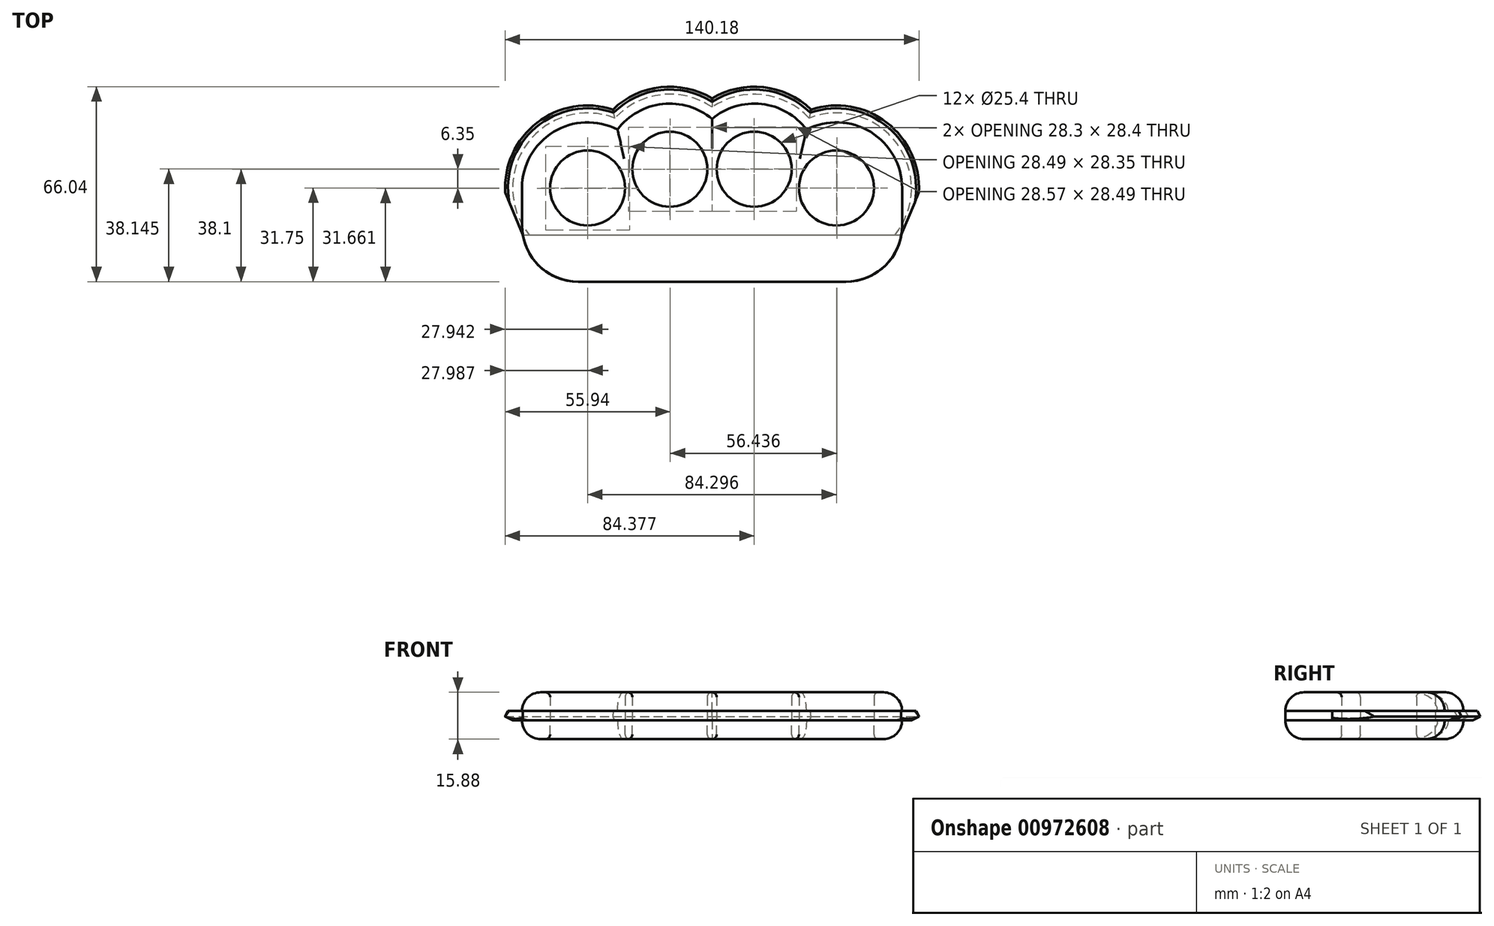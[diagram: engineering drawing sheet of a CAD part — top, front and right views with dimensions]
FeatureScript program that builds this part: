
annotation { "Feature Type Name" : "Feature", "Feature Type Description" : "" }
export const myFeature = defineFeature(function(context is Context, id is Id, definition is map)
    precondition{}
    {
        {
            var Q0;
            Q0=qCreatedBy(makeId("Top.planeOp"),FACE);
            var sketch = newSketch(context, id + "F0", { "sketchPlane" : qUnion([Q0])});
            skCircle(sketch, "E0", {"center": v(14.29, 38.1) * mm, "radius": 12.7 * mm});
            skPoint(sketch, "E1", {"position": v(14.29, 25.4) * mm});
            skCircle(sketch, "E2", {"center": v(42.15, 31.75) * mm, "radius": 12.7 * mm});
            skArc(sketch, "E3", {"start": v(0, 55.12) * mm, "mid": v(16.77, 60.19) * mm, "end": v(32, 51.52) * mm});
            skArc(sketch, "E4", {"start": v(32, 51.52) * mm, "mid": v(53.73, 50.72) * mm, "end": v(64.37, 31.75) * mm});
            skLineSegment(sketch, "E5", {"start": v(64.37, 31.75) * mm, "end": v(64.37, 19.05) * mm});
            skLineSegment(sketch, "E6", {"start": v(45.32, 0) * mm, "end": v(0, 0) * mm});
            skPoint(sketch, "E7.visualSharp", {"position": v(64.37, 0) * mm});
            skArc(sketch, "E7.filletArc", {"start": v(45.32, 0) * mm, "mid": v(58.8, 5.58) * mm, "end": v(64.37, 19.05) * mm});
            skLineSegment(sketch, "E8", {"start": v(0, 60.33) * mm, "end": v(0, 0) * mm, "construction": true});
            skLineSegment(sketch, "E9.MirrorCS", {"start": v(-45.32, 0) * mm, "end": v(0, 0) * mm});
            skCircle(sketch, "E10.MirrorC", {"center": v(-14.29, 38.1) * mm, "radius": 12.7 * mm});
            skArc(sketch, "E11.MirrorCS", {"start": v(0, 55.12) * mm, "mid": v(-16.77, 60.19) * mm, "end": v(-32, 51.52) * mm});
            skArc(sketch, "E12.MirrorCS", {"start": v(-32, 51.52) * mm, "mid": v(-53.73, 50.72) * mm, "end": v(-64.37, 31.75) * mm});
            skLineSegment(sketch, "E13.MirrorCS", {"start": v(-64.37, 31.75) * mm, "end": v(-64.37, 19.05) * mm});
            skArc(sketch, "E14.MirrorCS", {"start": v(-45.32, 0) * mm, "mid": v(-58.8, 5.58) * mm, "end": v(-64.37, 19.05) * mm});
            skCircle(sketch, "E15.MirrorC", {"center": v(-42.15, 31.75) * mm, "radius": 12.7 * mm});
            skPoint(sketch, "E16.MirrorCS.end.orphan", {"position": v(0, 60.33) * mm});
            skPoint(sketch, "E16.MirrorCS.start.orphan", {"position": v(0, 55.12) * mm});
            skPoint(sketch, "E17", {"position": v(14.29, 60.33) * mm});
            skSolve(sketch);
        }
        {
            var Q0;
            Q0 = qSketchRegion(id + "F0", true);
            extrude(context, id + "F1", {"entities" : qUnion([Q0]), "depth" : 7.94 * mm, "offsetDistance" : 25.4 * mm, "hasSecondDirection" : true, "secondDirectionOppositeDirection" : false, "secondDirectionDepth" : 1.59 * mm});
        }
        {
            var Q0;
            Q0=makeQuery(id+"F0.imprint","IMPRINT",FACE,{"disambiguationData":[TD([[makeQuery(id+"F0.imprint","IMPRINT",EDGE,{"derivedFrom":sQuery(id+"F0.wireOp",EDGE,"E0")}),-1.0]])]});
            extrude(context, id + "F2", {"entities" : qUnion([Q0]), "oppositeDirection" : true, "depth" : 7.94 * mm, "offsetDistance" : 25.4 * mm, "hasSecondDirection" : true, "secondDirectionOppositeDirection" : true, "secondDirectionDepth" : 1.59 * mm});
        }
        {
            var Q0;
            Q0=makeQuery(id+"F2.opExtrude","CAP_FACE",FACE,{"disambiguationData":[OSD([sQuery(id+"F0.wireOp",EDGE,"E0"),sQuery(id+"F0.wireOp",EDGE,"E2"),sQuery(id+"F0.wireOp",EDGE,"E3"),sQuery(id+"F0.wireOp",EDGE,"E4"),sQuery(id+"F0.wireOp",EDGE,"E5"),sQuery(id+"F0.wireOp",EDGE,"E6"),sQuery(id+"F0.wireOp",EDGE,"E7.filletArc"),sQuery(id+"F0.wireOp",EDGE,"E9.MirrorCS"),sQuery(id+"F0.wireOp",EDGE,"E10.MirrorC"),sQuery(id+"F0.wireOp",EDGE,"E11.MirrorCS"),sQuery(id+"F0.wireOp",EDGE,"E12.MirrorCS"),sQuery(id+"F0.wireOp",EDGE,"E13.MirrorCS"),sQuery(id+"F0.wireOp",EDGE,"E14.MirrorCS"),sQuery(id+"F0.wireOp",EDGE,"E15.MirrorC")])],"isStart":true});
            var sketch = newSketch(context, id + "F3", { "sketchPlane" : qUnion([Q0])});
            skLineSegment(sketch, "E18.bottom", {"start": v(-70.72, 15.87) * mm, "end": v(70.72, 15.87) * mm});
            skLineSegment(sketch, "E18.top", {"start": v(-70.72, 66.68) * mm, "end": v(70.72, 66.68) * mm, "construction": true});
            skLineSegment(sketch, "E18.left", {"start": v(-70.72, 15.87) * mm, "end": v(-70.72, 66.67) * mm, "construction": true});
            skLineSegment(sketch, "E18.right", {"start": v(70.72, 15.87) * mm, "end": v(70.72, 66.68) * mm, "construction": true});
            skPoint(sketch, "E18.middle", {"position": v(0, 41.27) * mm});
            skArc(sketch, "E19", {"start": v(0, 62.85) * mm, "mid": v(-17.48, 66.5) * mm, "end": v(-33.72, 59.05) * mm});
            skPoint(sketch, "E19.startSnap0", {"position": v(0, 66.68) * mm});
            skArc(sketch, "E20", {"start": v(-70.72, 31.75) * mm, "mid": v(-59.11, 54.74) * mm, "end": v(-33.72, 59.05) * mm});
            skLineSegment(sketch, "E21", {"start": v(-64.1, 15.87) * mm, "end": v(-70.72, 31.75) * mm});
            skLineSegment(sketch, "E22", {"start": v(0, 66.68) * mm, "end": v(0, 15.87) * mm, "construction": true});
            skArc(sketch, "E23.MirrorCS", {"start": v(0, 62.85) * mm, "mid": v(17.48, 66.5) * mm, "end": v(33.72, 59.05) * mm});
            skArc(sketch, "E24.MirrorCS", {"start": v(70.72, 31.75) * mm, "mid": v(59.11, 54.74) * mm, "end": v(33.72, 59.05) * mm});
            skLineSegment(sketch, "E25.MirrorCS", {"start": v(64.1, 15.87) * mm, "end": v(70.72, 31.75) * mm});
            skCircle(sketch, "E26", {"center": v(-42.15, 31.75) * mm, "radius": 12.7 * mm});
            skCircle(sketch, "E27", {"center": v(-14.29, 38.1) * mm, "radius": 12.7 * mm});
            skCircle(sketch, "E28.MirrorC", {"center": v(14.29, 38.1) * mm, "radius": 12.7 * mm});
            skCircle(sketch, "E29.MirrorC", {"center": v(42.15, 31.75) * mm, "radius": 12.7 * mm});
            skSolve(sketch);
        }
        {
            var Q0;
            Q0 = qSketchRegion(id + "F3", true);
            extrude(context, id + "F4", {"entities" : qUnion([Q0]), "depth" : 3.17 * mm, "offsetDistance" : 25.4 * mm});
        }
        {
            var Q0;
            Q0=makeQuery(id+"F4.opExtrude","CAP_EDGE",EDGE,{"disambiguationData":[OSD([sQuery(id+"F3.wireOp",EDGE,"E19")])],"isStart":true});
            var Q1;
            Q1=makeQuery(id+"F4.opExtrude","CAP_EDGE",EDGE,{"disambiguationData":[OSD([sQuery(id+"F3.wireOp",EDGE,"E20")])],"isStart":true});
            var Q2;
            Q2=makeQuery(id+"F4.opExtrude","CAP_EDGE",EDGE,{"disambiguationData":[OSD([sQuery(id+"F3.wireOp",EDGE,"E23.MirrorCS")])],"isStart":true});
            var Q3;
            Q3=makeQuery(id+"F4.opExtrude","CAP_EDGE",EDGE,{"disambiguationData":[OSD([sQuery(id+"F3.wireOp",EDGE,"E24.MirrorCS")])],"isStart":true});
            chamfer(context, id + "F5", {"entities" : qUnion([Q0, Q1, Q2, Q3]), "chamferType" : ChamferType.TWO_OFFSETS, "width1" : 1.59 * mm, "oppositeDirection" : false, "width2" : 3.17 * mm, "tangentPropagation" : true});
        }
        {
            var Q0;
            Q0=makeQuery(id+"F4.opExtrude","CAP_EDGE",EDGE,{"disambiguationData":[OSD([sQuery(id+"F3.wireOp",EDGE,"E20")])],"isStart":false});
            var Q1;
            Q1=makeQuery(id+"F4.opExtrude","CAP_EDGE",EDGE,{"disambiguationData":[OSD([sQuery(id+"F3.wireOp",EDGE,"E19")])],"isStart":false});
            var Q2;
            Q2=makeQuery(id+"F4.opExtrude","CAP_EDGE",EDGE,{"disambiguationData":[OSD([sQuery(id+"F3.wireOp",EDGE,"E23.MirrorCS")])],"isStart":false});
            var Q3;
            Q3=makeQuery(id+"F4.opExtrude","CAP_EDGE",EDGE,{"disambiguationData":[OSD([sQuery(id+"F3.wireOp",EDGE,"E24.MirrorCS")])],"isStart":false});
            chamfer(context, id + "F6", {"entities" : qUnion([Q0, Q1, Q2, Q3]), "chamferType" : ChamferType.TWO_OFFSETS, "width1" : 1.59 * mm, "oppositeDirection" : false, "width2" : 3.17 * mm, "tangentPropagation" : true});
        }
        {
            var Q0;
            {var subQ5=makeQuery(id+"F2.opExtrude","CAP_EDGE",EDGE,{"disambiguationData":[OSD([sQuery(id+"F0.wireOp",EDGE,"E6"),sQuery(id+"F0.wireOp",EDGE,"E9.MirrorCS")])],"isStart":true});Q0=makeQuery(id+"F3.imprint","IMPRINT",FACE,{"disambiguationData":[TD([[makeQuery(id+"F3.imprint","IMPRINT",EDGE,{"derivedFrom":subQ5}),1.0]])]});}
            extrude(context, id + "F7", {"entities" : qUnion([Q0]), "depth" : 3.17 * mm, "offsetDistance" : 25.4 * mm});
        }
        {
            var Q0;
            Q0=makeQuery(id+"F1.opExtrude","CAP_EDGE",EDGE,{"disambiguationData":[OSD([sQuery(id+"F0.wireOp",EDGE,"E14.MirrorCS")])],"isStart":false});
            var Q1;
            Q1=makeQuery(id+"F1.opExtrude","CAP_EDGE",EDGE,{"disambiguationData":[OSD([sQuery(id+"F0.wireOp",EDGE,"E13.MirrorCS")])],"isStart":false});
            var Q2;
            Q2=makeQuery(id+"F1.opExtrude","CAP_EDGE",EDGE,{"disambiguationData":[OSD([sQuery(id+"F0.wireOp",EDGE,"E12.MirrorCS")])],"isStart":false});
            var Q3;
            Q3=makeQuery(id+"F1.opExtrude","CAP_EDGE",EDGE,{"disambiguationData":[OSD([sQuery(id+"F0.wireOp",EDGE,"E11.MirrorCS")])],"isStart":false});
            var Q4;
            Q4=makeQuery(id+"F1.opExtrude","CAP_EDGE",EDGE,{"disambiguationData":[OSD([sQuery(id+"F0.wireOp",EDGE,"E3")])],"isStart":false});
            var Q5;
            Q5=makeQuery(id+"F1.opExtrude","CAP_EDGE",EDGE,{"disambiguationData":[OSD([sQuery(id+"F0.wireOp",EDGE,"E4")])],"isStart":false});
            var Q6;
            Q6=makeQuery(id+"F1.opExtrude","CAP_EDGE",EDGE,{"disambiguationData":[OSD([sQuery(id+"F0.wireOp",EDGE,"E7.filletArc")])],"isStart":false});
            var Q7;
            Q7=makeQuery(id+"F1.opExtrude","CAP_EDGE",EDGE,{"disambiguationData":[OSD([sQuery(id+"F0.wireOp",EDGE,"E5")])],"isStart":false});
            var Q8;
            Q8=makeQuery(id+"F1.opExtrude","CAP_EDGE",EDGE,{"disambiguationData":[OSD([sQuery(id+"F0.wireOp",EDGE,"E6"),sQuery(id+"F0.wireOp",EDGE,"E9.MirrorCS")])],"isStart":false});
            var Q9;
            Q9=makeQuery(id+"F2.opExtrude","CAP_EDGE",EDGE,{"disambiguationData":[OSD([sQuery(id+"F0.wireOp",EDGE,"E6"),sQuery(id+"F0.wireOp",EDGE,"E9.MirrorCS")])],"isStart":false});
            var Q10;
            Q10=makeQuery(id+"F2.opExtrude","CAP_EDGE",EDGE,{"disambiguationData":[OSD([sQuery(id+"F0.wireOp",EDGE,"E13.MirrorCS")])],"isStart":false});
            var Q11;
            Q11=makeQuery(id+"F2.opExtrude","CAP_EDGE",EDGE,{"disambiguationData":[OSD([sQuery(id+"F0.wireOp",EDGE,"E11.MirrorCS")])],"isStart":false});
            var Q12;
            Q12=makeQuery(id+"F2.opExtrude","CAP_EDGE",EDGE,{"disambiguationData":[OSD([sQuery(id+"F0.wireOp",EDGE,"E12.MirrorCS")])],"isStart":false});
            var Q13;
            Q13=makeQuery(id+"F2.opExtrude","CAP_EDGE",EDGE,{"disambiguationData":[OSD([sQuery(id+"F0.wireOp",EDGE,"E14.MirrorCS")])],"isStart":false});
            var Q14;
            Q14=makeQuery(id+"F2.opExtrude","CAP_EDGE",EDGE,{"disambiguationData":[OSD([sQuery(id+"F0.wireOp",EDGE,"E3")])],"isStart":false});
            var Q15;
            Q15=makeQuery(id+"F2.opExtrude","CAP_EDGE",EDGE,{"disambiguationData":[OSD([sQuery(id+"F0.wireOp",EDGE,"E4")])],"isStart":false});
            var Q16;
            Q16=makeQuery(id+"F2.opExtrude","CAP_EDGE",EDGE,{"disambiguationData":[OSD([sQuery(id+"F0.wireOp",EDGE,"E5")])],"isStart":false});
            var Q17;
            Q17=makeQuery(id+"F2.opExtrude","CAP_EDGE",EDGE,{"disambiguationData":[OSD([sQuery(id+"F0.wireOp",EDGE,"E7.filletArc")])],"isStart":false});
            fillet(context, id + "F8", {"entities" : qUnion([Q0, Q1, Q2, Q3, Q4, Q5, Q6, Q7, Q8, Q9, Q10, Q11, Q12, Q13, Q14, Q15, Q16, Q17]), "radius" : 6.35 * mm, "tangentPropagation" : true, "allowEdgeOverflow" : false});
        }
        {
            var Q0;
            Q0=makeQuery(id+"F2.opExtrude","CAP_EDGE",EDGE,{"disambiguationData":[OSD([sQuery(id+"F0.wireOp",EDGE,"E15.MirrorC")])],"isStart":false});
            var Q1;
            Q1=makeQuery(id+"F2.opExtrude","CAP_EDGE",EDGE,{"disambiguationData":[OSD([sQuery(id+"F0.wireOp",EDGE,"E10.MirrorC")])],"isStart":false});
            var Q2;
            Q2=makeQuery(id+"F2.opExtrude","CAP_EDGE",EDGE,{"disambiguationData":[OSD([sQuery(id+"F0.wireOp",EDGE,"E0")])],"isStart":false});
            var Q3;
            Q3=makeQuery(id+"F2.opExtrude","CAP_EDGE",EDGE,{"disambiguationData":[OSD([sQuery(id+"F0.wireOp",EDGE,"E2")])],"isStart":false});
            var Q4;
            Q4=makeQuery(id+"F1.opExtrude","CAP_EDGE",EDGE,{"disambiguationData":[OSD([sQuery(id+"F0.wireOp",EDGE,"E2")])],"isStart":false});
            var Q5;
            Q5=makeQuery(id+"F1.opExtrude","CAP_EDGE",EDGE,{"disambiguationData":[OSD([sQuery(id+"F0.wireOp",EDGE,"E0")])],"isStart":false});
            var Q6;
            Q6=makeQuery(id+"F1.opExtrude","CAP_EDGE",EDGE,{"disambiguationData":[OSD([sQuery(id+"F0.wireOp",EDGE,"E10.MirrorC")])],"isStart":false});
            var Q7;
            Q7=makeQuery(id+"F1.opExtrude","CAP_EDGE",EDGE,{"disambiguationData":[OSD([sQuery(id+"F0.wireOp",EDGE,"E15.MirrorC")])],"isStart":false});
            fillet(context, id + "F9", {"entities" : qUnion([Q0, Q1, Q2, Q3, Q4, Q5, Q6, Q7]), "radius" : 1.59 * mm, "tangentPropagation" : true, "allowEdgeOverflow" : false});
        }
    });
